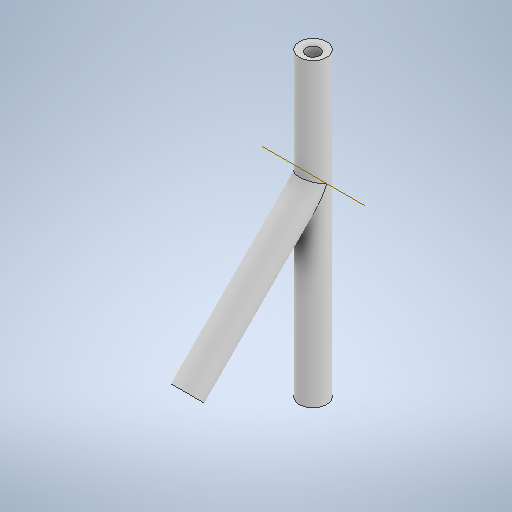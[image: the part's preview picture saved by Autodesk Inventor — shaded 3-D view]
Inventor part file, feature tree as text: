
AUTODESK INVENTOR PART (.ipt)
format: ipt  version: 2025 (Build 290162000, 162)  size: 279,552 bytes
history: native  units: mm
features: extrude x5, sketch x5, other x2, chamfer x1
ambient origin geometry x8: Origin, YZ Plane, XZ Plane, XY Plane, X Axis, Y Axis, Z Axis, Center Point
bodies: Body1 (feature_tree)
feature tree (13):
  other  "Bryła1"
  other  "Płaszczyzna konstrukcyjna9"
  extrude  "Wyciągnięcie proste1"  Depth=10.0mm
  extrude  "Wyciągnięcie proste2"  Depth=65.0mm TaperAngle=0.0deg
  extrude  "Wyciągnięcie proste3"  Depth=10.0mm
  extrude  "Wyciągnięcie proste4"  Depth=140.0mm TaperAngle=0.0deg
  extrude  "Wyciągnięcie proste5"  Depth=7.0mm
  chamfer  "Faza1"  Distance=60.0mm
  sketch  "Szkic5"
  sketch  "Szkic6"
  sketch  "Szkic8"
  sketch  "Szkic9"
  sketch  "Szkic10"
